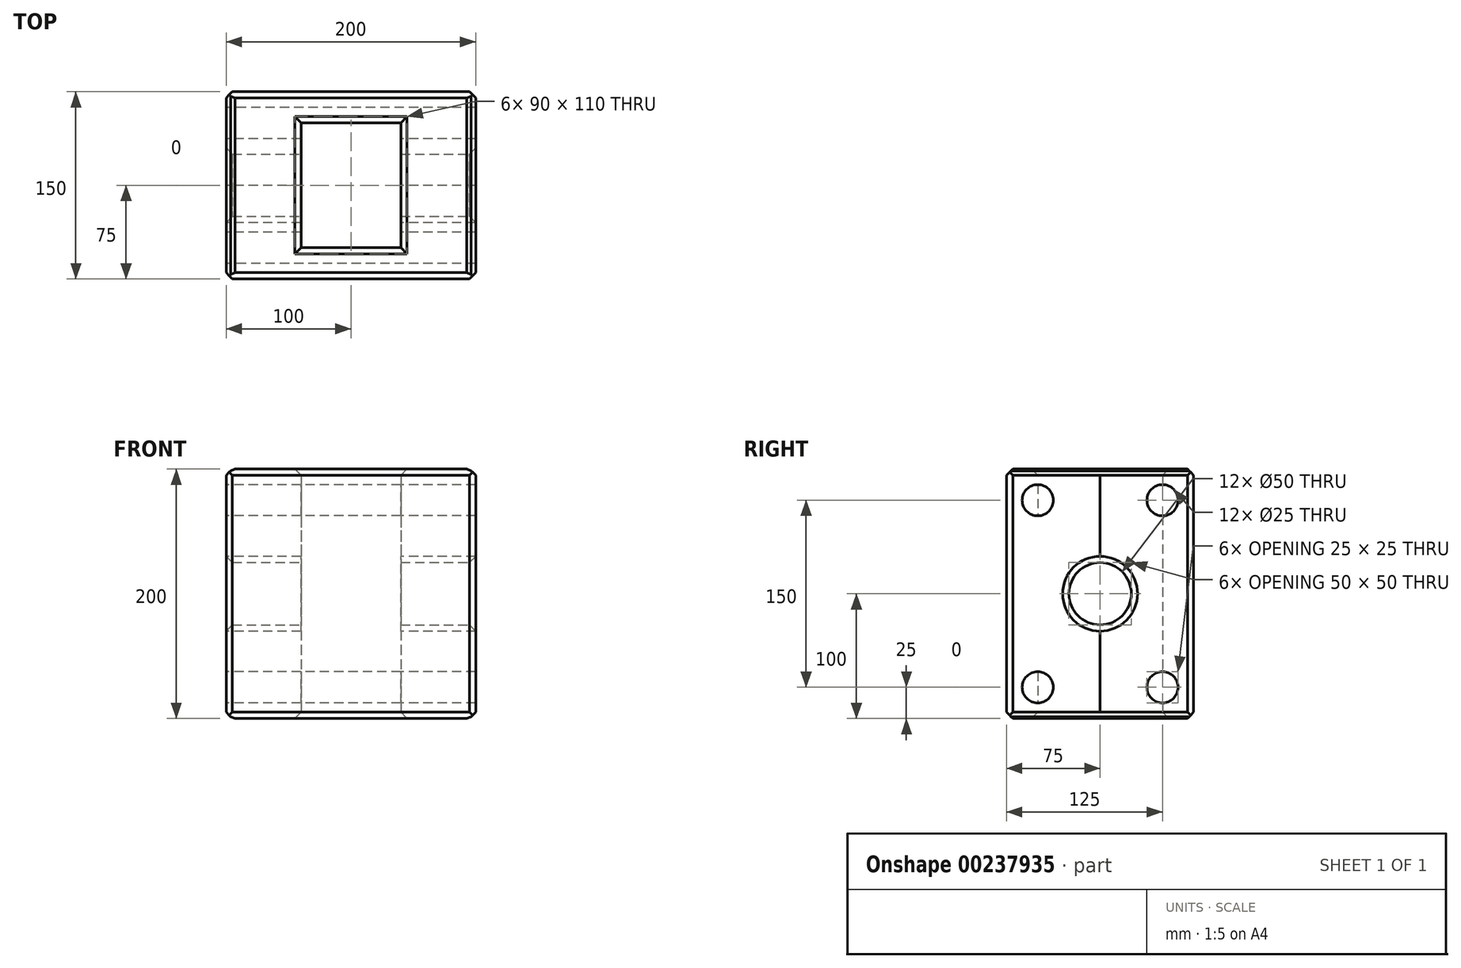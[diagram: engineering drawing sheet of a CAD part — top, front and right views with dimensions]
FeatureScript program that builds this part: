
annotation { "Feature Type Name" : "Feature", "Feature Type Description" : "" }
export const myFeature = defineFeature(function(context is Context, id is Id, definition is map)
    precondition{}
    {
        {
            var Q0;
            Q0=qCreatedBy(makeId("Right.planeOp"),FACE);
            var sketch = newSketch(context, id + "F0", { "sketchPlane" : qUnion([Q0])});
            skLineSegment(sketch, "E0.bottom", {"start": v(75, -100) * mm, "end": v(-75, -100) * mm});
            skLineSegment(sketch, "E0.top", {"start": v(75, 100) * mm, "end": v(-75, 100) * mm});
            skLineSegment(sketch, "E0.left", {"start": v(75, -100) * mm, "end": v(75, 100) * mm});
            skLineSegment(sketch, "E0.right", {"start": v(-75, -100) * mm, "end": v(-75, 100) * mm});
            skPoint(sketch, "E0.middle", {"position": v(0, 0) * mm});
            skCircle(sketch, "E1", {"center": v(0, 0) * mm, "radius": 25 * mm});
            skSolve(sketch);
        }
        {
            var Q0;
            Q0=makeQuery(id+"F0.imprint","IMPRINT",FACE,{"disambiguationData":[TD([[makeQuery(id+"F0.imprint","IMPRINT",EDGE,{"derivedFrom":sQuery(id+"F0.wireOp",EDGE,"E0.bottom")}),-1.0]])]});
            extrude(context, id + "F1", {"entities" : qUnion([Q0]), "oppositeDirection" : true, "depth" : 200 * mm});
        }
        {
            var Q0;
            Q0=makeQuery(id+"F1.opExtrude","CAP_FACE",FACE,{"disambiguationData":[OSD([sQuery(id+"F0.wireOp",EDGE,"E0.bottom"),sQuery(id+"F0.wireOp",EDGE,"E0.top"),sQuery(id+"F0.wireOp",EDGE,"E0.left"),sQuery(id+"F0.wireOp",EDGE,"E0.right"),sQuery(id+"F0.wireOp",EDGE,"E1")])],"isStart":true});
            var Q1;
            Q1=makeQuery(id+"F1.opExtrude","CAP_FACE",FACE,{"disambiguationData":[OSD([sQuery(id+"F0.wireOp",EDGE,"E0.bottom"),sQuery(id+"F0.wireOp",EDGE,"E0.top"),sQuery(id+"F0.wireOp",EDGE,"E0.left"),sQuery(id+"F0.wireOp",EDGE,"E0.right"),sQuery(id+"F0.wireOp",EDGE,"E1")])],"isStart":false});
            chamfer(context, id + "F2", {"entities" : qUnion([Q0, Q1]), "width" : 5 * mm, "tangentPropagation" : true});
        }
        {
            var Q0;
            Q0=makeQuery(id+"F1.opExtrude","CAP_FACE",FACE,{"disambiguationData":[OSD([sQuery(id+"F0.wireOp",EDGE,"E0.bottom"),sQuery(id+"F0.wireOp",EDGE,"E0.top"),sQuery(id+"F0.wireOp",EDGE,"E0.left"),sQuery(id+"F0.wireOp",EDGE,"E0.right"),sQuery(id+"F0.wireOp",EDGE,"E1")])],"isStart":false});
            var sketch = newSketch(context, id + "F3", { "sketchPlane" : qUnion([Q0])});
            skCircle(sketch, "E2", {"center": v(-50, 75) * mm, "radius": 12.5 * mm});
            skCircle(sketch, "E3", {"center": v(-50, -75) * mm, "radius": 12.5 * mm});
            skLineSegment(sketch, "E4", {"start": v(0, -95) * mm, "end": v(0, 95) * mm});
            skCircle(sketch, "E5.MirrorC", {"center": v(50, -75) * mm, "radius": 12.5 * mm});
            skCircle(sketch, "E6.MirrorC", {"center": v(50, 75) * mm, "radius": 12.5 * mm});
            skSolve(sketch);
        }
        {
            var Q0;
            Q0=makeQuery(id+"F3.imprint","IMPRINT",FACE,{"disambiguationData":[TD([[makeQuery(id+"F3.imprint","IMPRINT",EDGE,{"derivedFrom":sQuery(id+"F3.wireOp",EDGE,"E3")}),1.0]])]});
            var Q1;
            Q1=makeQuery(id+"F3.imprint","IMPRINT",FACE,{"disambiguationData":[TD([[makeQuery(id+"F3.imprint","IMPRINT",EDGE,{"derivedFrom":sQuery(id+"F3.wireOp",EDGE,"E2")}),1.0]])]});
            var Q2;
            Q2=makeQuery(id+"F3.imprint","IMPRINT",FACE,{"disambiguationData":[TD([[makeQuery(id+"F3.imprint","IMPRINT",EDGE,{"derivedFrom":sQuery(id+"F3.wireOp",EDGE,"E5.MirrorC")}),-1.0]])]});
            var Q3;
            Q3=makeQuery(id+"F3.imprint","IMPRINT",FACE,{"disambiguationData":[TD([[makeQuery(id+"F3.imprint","IMPRINT",EDGE,{"derivedFrom":sQuery(id+"F3.wireOp",EDGE,"E6.MirrorC")}),-1.0]])]});
            extrude(context, id + "F4", {"entities" : qUnion([Q0, Q1, Q2, Q3]), "operationType" : NewBodyOperationType.REMOVE, "endBound" : BoundingType.THROUGH_ALL, "oppositeDirection" : true, "depth" : 25 * mm});
        }
        {
            var Q0;
            Q0=makeQuery(id+"F1.opExtrude","SWEPT_FACE",FACE,{"disambiguationData":[OSD([sQuery(id+"F0.wireOp",EDGE,"E0.bottom")])]});
            var sketch = newSketch(context, id + "F5", { "sketchPlane" : qUnion([Q0])});
            skLineSegment(sketch, "E7.bottom", {"start": v(-60, 50) * mm, "end": v(-140, 50) * mm});
            skLineSegment(sketch, "E7.top", {"start": v(-60, -50) * mm, "end": v(-140, -50) * mm});
            skLineSegment(sketch, "E7.left", {"start": v(-60, 50) * mm, "end": v(-60, -50) * mm});
            skLineSegment(sketch, "E7.right", {"start": v(-140, 50) * mm, "end": v(-140, -50) * mm});
            skPoint(sketch, "E7.middle", {"position": v(-100, 0) * mm});
            skSolve(sketch);
        }
        {
            var Q0;
            Q0=makeQuery(id+"F5.imprint","IMPRINT",FACE,{"disambiguationData":[TD([[makeQuery(id+"F5.imprint","IMPRINT",EDGE,{"derivedFrom":sQuery(id+"F5.wireOp",EDGE,"E7.bottom")}),1.0]])]});
            extrude(context, id + "F6", {"entities" : qUnion([Q0]), "operationType" : NewBodyOperationType.REMOVE, "endBound" : BoundingType.THROUGH_ALL, "oppositeDirection" : true, "depth" : 25 * mm});
        }
        {
            var Q0;
            Q0=makeQuery(id+"F1.opExtrude","SWEPT_FACE",FACE,{"disambiguationData":[OSD([sQuery(id+"F0.wireOp",EDGE,"E0.bottom")])]});
            var Q1;
            Q1=makeQuery(id+"F1.opExtrude","SWEPT_FACE",FACE,{"disambiguationData":[OSD([sQuery(id+"F0.wireOp",EDGE,"E0.top")])]});
            chamfer(context, id + "F7", {"entities" : qUnion([Q0, Q1]), "width" : 5 * mm, "tangentPropagation" : true});
        }
    });
